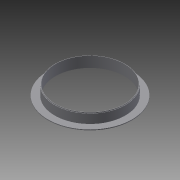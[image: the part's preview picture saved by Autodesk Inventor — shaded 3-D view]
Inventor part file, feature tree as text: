
AUTODESK INVENTOR PART (.ipt)
format: ipt  version: 2015 (Build 190159000, 159)  size: 100,864 bytes
history: native  units: in
note: dims shown in document units (in); Inventor stores cm internally (conversion verified against a paired STEP export)
features: revolve x1, sketch x1
ambient origin geometry x8: Origin, YZ Plane, XZ Plane, XY Plane, X Axis, Y Axis, Z Axis, Center Point
bodies: Solid1 (feature_tree)
feature tree (2):
  revolve  "Revolution1"  Angle=90.0deg
  sketch  "Sketch1"  dims[d0=1.25in d1=0.125in d2=1.125in d3=4.375in d4=0.125in d5=5.75in d6=0.125in d7=0.5in d8=1.625in d9=0.125in d10=90.0deg]
